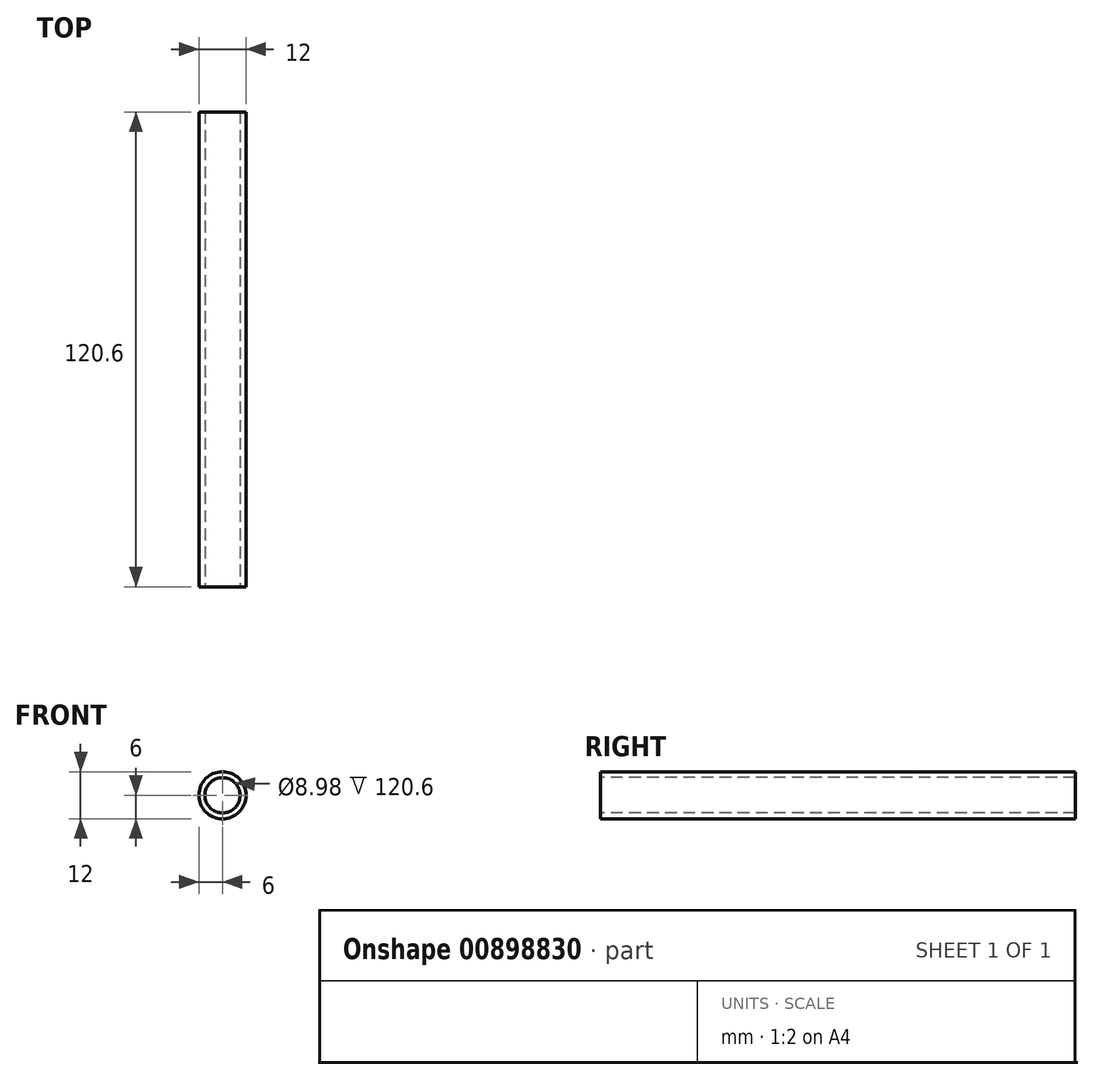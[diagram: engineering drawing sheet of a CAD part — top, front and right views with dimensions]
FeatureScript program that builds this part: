
annotation { "Feature Type Name" : "Feature", "Feature Type Description" : "" }
export const myFeature = defineFeature(function(context is Context, id is Id, definition is map)
    precondition{}
    {
        {
            var Q0;
            Q0=qCreatedBy(makeId("Front.planeOp"),FACE);
            var sketch = newSketch(context, id + "F0", { "sketchPlane" : qUnion([Q0])});
            skCircle(sketch, "E0", {"center": v(0, 0) * mm, "radius": 4.7 * mm});
            skCircle(sketch, "E1", {"center": v(0, 0) * mm, "radius": 5.7 * mm});
            skSolve(sketch);
        }
        {
            var Q0;
            Q0=makeQuery(id+"F0.imprint","IMPRINT",FACE,{"disambiguationData":[TD([[makeQuery(id+"F0.imprint","IMPRINT",EDGE,{"derivedFrom":sQuery(id+"F0.wireOp",EDGE,"E0")}),-1.0]])]});
            extrude(context, id + "F1", {"entities" : qUnion([Q0]), "oppositeDirection" : true, "depth" : 120 * mm, "offsetDistance" : 25 * mm});
        }
        {
            var Q0;
            Q0=qCreatedBy(makeId("Front.planeOp"),FACE);
            var sketch = newSketch(context, id + "F2", { "sketchPlane" : qUnion([Q0])});
            skCircle(sketch, "E2", {"center": v(0, 0) * mm, "radius": 4.49 * mm});
            skCircle(sketch, "E3", {"center": v(0, 0) * mm, "radius": 6 * mm});
            skSolve(sketch);
        }
        {
            var Q0;
            Q0=makeQuery(id+"F2.imprint","IMPRINT",FACE,{"disambiguationData":[TD([[makeQuery(id+"F2.imprint","IMPRINT",EDGE,{"derivedFrom":sQuery(id+"F2.wireOp",EDGE,"E2")}),-1.0]])]});
            extrude(context, id + "F3", {"entities" : qUnion([Q0]), "operationType" : NewBodyOperationType.ADD, "oppositeDirection" : true, "depth" : 120.6 * mm, "offsetDistance" : 25 * mm});
        }
    });
